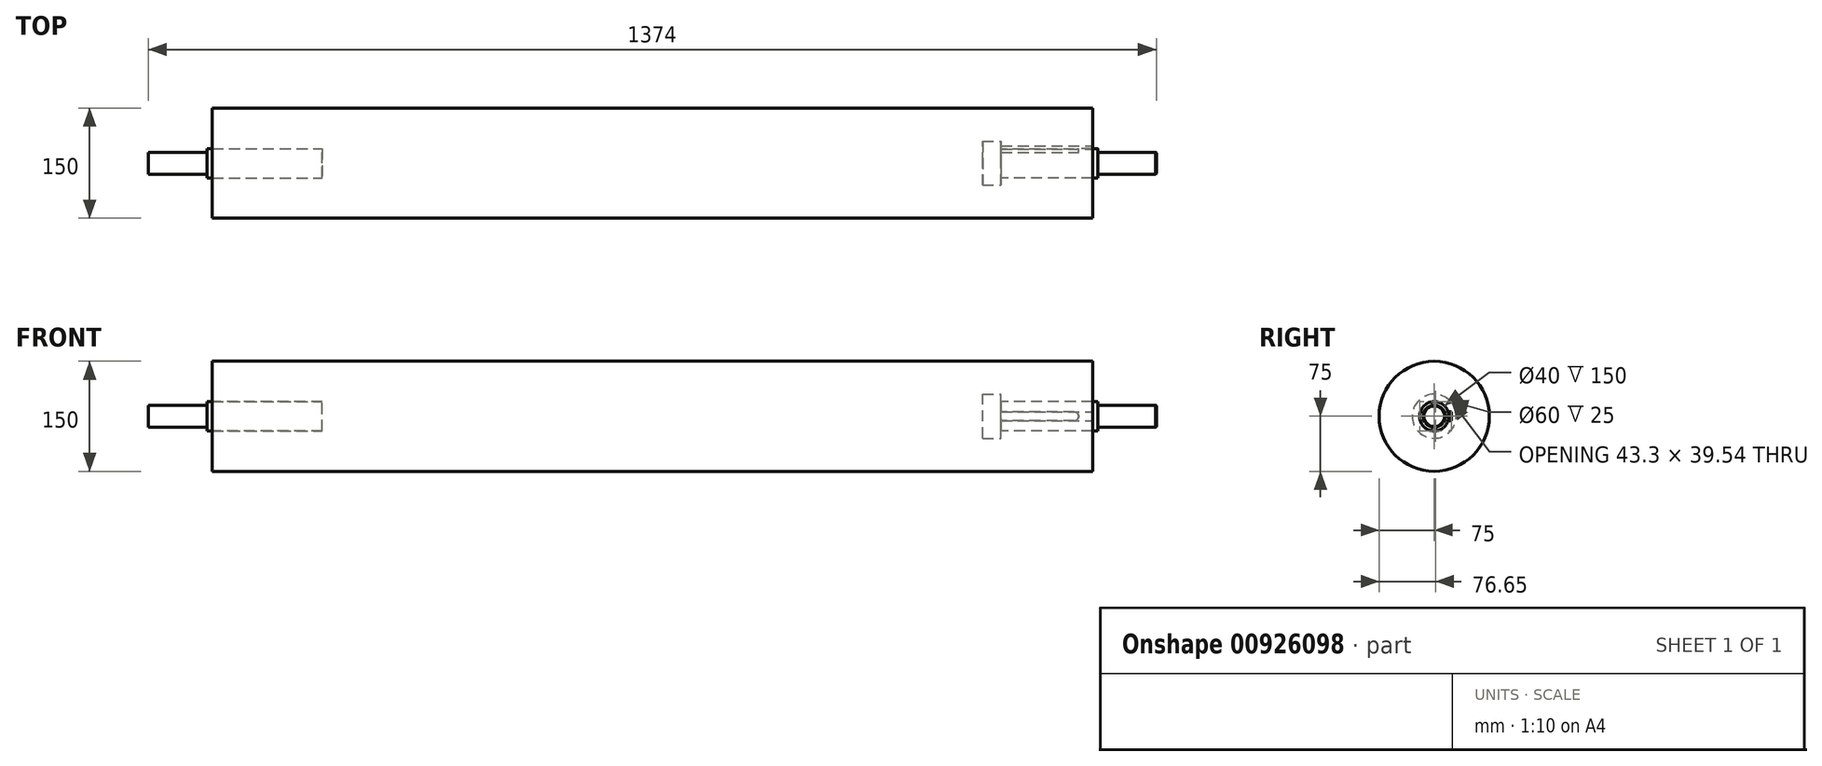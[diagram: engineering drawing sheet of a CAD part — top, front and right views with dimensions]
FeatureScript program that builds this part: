
annotation { "Feature Type Name" : "Feature", "Feature Type Description" : "" }
export const myFeature = defineFeature(function(context is Context, id is Id, definition is map)
    precondition{}
    {
        {
            var Q0;
            Q0=qCreatedBy(makeId("Right.planeOp"),FACE);
            var sketch = newSketch(context, id + "F0", { "sketchPlane" : qUnion([Q0])});
            skCircle(sketch, "E0", {"center": v(0, 0) * mm, "radius": 75 * mm});
            skSolve(sketch);
        }
        {
            var Q0;
            Q0=qSketchRegion(id+"F0",true);
            extrude(context, id + "F1", {"entities" : qUnion([Q0]), "endBound" : BoundingType.SYMMETRIC, "depth" : 1200 * mm, "offsetDistance" : 25 * mm});
        }
        {
            var Q0;
            Q0=makeQuery(id+"F1.opExtrude","CAP_FACE",FACE,{"disambiguationData":[OSD([sQuery(id+"F0.wireOp",EDGE,"E0")])],"isStart":false});
            var sketch = newSketch(context, id + "F2", { "sketchPlane" : qUnion([Q0])});
            skCircle(sketch, "E1", {"center": v(0, 0) * mm, "radius": 20 * mm});
            skSolve(sketch);
        }
        {
            var Q0;
            Q0=qSketchRegion(id+"F2",true);
            extrude(context, id + "F3", {"entities" : qUnion([Q0]), "operationType" : NewBodyOperationType.REMOVE, "oppositeDirection" : true, "depth" : 150 * mm, "offsetDistance" : 25 * mm});
        }
        {
            var Q0;
            Q0=makeQuery(id+"F1.opExtrude","CAP_FACE",FACE,{"disambiguationData":[OSD([sQuery(id+"F0.wireOp",EDGE,"E0")])],"isStart":true});
            var sketch = newSketch(context, id + "F4", { "sketchPlane" : qUnion([Q0])});
            skCircle(sketch, "E2", {"center": v(0, 0) * mm, "radius": 20 * mm});
            skSolve(sketch);
        }
        {
            var Q0;
            Q0=qSketchRegion(id+"F4",true);
            extrude(context, id + "F5", {"entities" : qUnion([Q0]), "operationType" : NewBodyOperationType.REMOVE, "oppositeDirection" : true, "depth" : 150 * mm, "offsetDistance" : 25 * mm});
        }
        {
            var Q0;
            Q0=makeQuery(id+"F1.opExtrude","CAP_FACE",FACE,{"disambiguationData":[OSD([sQuery(id+"F0.wireOp",EDGE,"E0")])],"isStart":false});
            var sketch = newSketch(context, id + "F6", { "sketchPlane" : qUnion([Q0])});
            skLineSegment(sketch, "E3.bottom", {"start": v(19.08, 6) * mm, "end": v(23.3, 6) * mm});
            skLineSegment(sketch, "E3.top", {"start": v(19.08, -6) * mm, "end": v(23.3, -6) * mm});
            skLineSegment(sketch, "E3.left", {"start": v(19.08, 6) * mm, "end": v(19.08, -6) * mm});
            skLineSegment(sketch, "E3.right", {"start": v(23.3, 6) * mm, "end": v(23.3, -6) * mm});
            skPoint(sketch, "E3.middle", {"position": v(21.19, 0) * mm});
            skSolve(sketch);
        }
        {
            var Q0;
            Q0=qSketchRegion(id+"F6",true);
            extrude(context, id + "F7", {"entities" : qUnion([Q0]), "operationType" : NewBodyOperationType.REMOVE, "oppositeDirection" : true, "depth" : 125 * mm, "offsetDistance" : 25 * mm});
        }
        {
            var Q0;
            Q0=makeQuery(id+"F3.boolean.opBoolean","COPY",FACE,{"derivedFrom":makeQuery(id+"F3.opExtrude","CAP_FACE",FACE,{"disambiguationData":[OSD([sQuery(id+"F2.wireOp",EDGE,"E1")])],"isStart":false})});
            var sketch = newSketch(context, id + "F8", { "sketchPlane" : qUnion([Q0])});
            skCircle(sketch, "E4", {"center": v(0, 0) * mm, "radius": 20 * mm});
            skSolve(sketch);
        }
        {
            var Q0;
            Q0=qSketchRegion(id+"F8",true);
            extrude(context, id + "F9", {"entities" : qUnion([Q0]), "depth" : (182 - 25) * mm, "offsetDistance" : 25 * mm});
        }
        {
            var Q0;
            Q0=makeQuery(id+"F9.opExtrude","CAP_FACE",FACE,{"disambiguationData":[OSD([sQuery(id+"F8.wireOp",EDGE,"E4")])],"isStart":false});
            var sketch = newSketch(context, id + "F10", { "sketchPlane" : qUnion([Q0])});
            skCircle(sketch, "E5", {"center": v(0, 0) * mm, "radius": 15 * mm});
            skSolve(sketch);
        }
        {
            var Q0;
            Q0=qSketchRegion(id+"F10",true);
            extrude(context, id + "F11", {"entities" : qUnion([Q0]), "operationType" : NewBodyOperationType.ADD, "depth" : 80 * mm, "offsetDistance" : 25 * mm});
        }
        {
            var Q0;
            Q0=makeQuery(id+"F9.opExtrude","SWEPT_BODY",BODY,{"disambiguationData":[OSD([sQuery(id+"F8.wireOp",EDGE,"E4")])]});
            var Q1;
            Q1=qCreatedBy(makeId("Right.planeOp"),FACE);
            mirror(context, id + "F12", {"entities" : qUnion([Q0]), "mirrorPlane" : qUnion([Q1])});
        }
        {
            var Q0;
            Q0=makeQuery(id+"F7.boolean.opBoolean","COPY",FACE,{"derivedFrom":makeQuery(id+"F7.opExtrude","SWEPT_FACE",FACE,{"disambiguationData":[OSD([sQuery(id+"F6.wireOp",EDGE,"E3.right")])]})});
            var sketch = newSketch(context, id + "F13", { "sketchPlane" : qUnion([Q0])});
            skLineSegment(sketch, "E6", {"start": v(475, 0) * mm, "end": v(575, 0) * mm});
            skArc(sketch, "E7.0.startCap", {"start": v(475, -6) * mm, "mid": v(469, 0) * mm, "end": v(475, 6) * mm});
            skArc(sketch, "E7.0.endCap", {"start": v(575, 6) * mm, "mid": v(581, 0) * mm, "end": v(575, -6) * mm});
            skLineSegment(sketch, "E7.0.left", {"start": v(475, 6) * mm, "end": v(575, 6) * mm});
            skLineSegment(sketch, "E7.0.right", {"start": v(475, -6) * mm, "end": v(575, -6) * mm});
            skSolve(sketch);
        }
        {
            var Q0;
            Q0=qSketchRegion(id+"F13",true);
            extrude(context, id + "F14", {"entities" : qUnion([Q0]), "operationType" : NewBodyOperationType.REMOVE, "depth" : 8.8 * mm, "offsetDistance" : 25 * mm});
        }
        {
            var Q0;
            Q0=makeQuery(id+"F1.opExtrude","CAP_FACE",FACE,{"disambiguationData":[OSD([sQuery(id+"F0.wireOp",EDGE,"E0")])],"isStart":false});
            cPlane(context, id + "F15", {"entities" : qUnion([Q0]), "cplaneType" : CPlaneType.OFFSET, "offset" : 125 * mm, "oppositeDirection" : true, "width" : 150 * mm, "height" : 150 * mm});
        }
        {
            var Q0;
            Q0=qCreatedBy(id+"F15.planeOp",FACE);
            var sketch = newSketch(context, id + "F16", { "sketchPlane" : qUnion([Q0])});
            skCircle(sketch, "E8", {"center": v(0, 0) * mm, "radius": 30 * mm});
            skSolve(sketch);
        }
        {
            var Q0;
            Q0=qSketchRegion(id+"F16",true);
            extrude(context, id + "F17", {"entities" : qUnion([Q0]), "operationType" : NewBodyOperationType.REMOVE, "oppositeDirection" : true, "depth" : 25 * mm, "offsetDistance" : 25 * mm});
        }
        {
            var Q0;
            Q0=makeQuery(id+"F12.opPattern","COPY",FACE,{"derivedFrom":makeQuery(id+"F11.opExtrude","CAP_FACE",FACE,{"disambiguationData":[OSD([sQuery(id+"F10.wireOp",EDGE,"E5")])],"isStart":false}),"instanceName":"1"});
            extrude(context, id + "F18", {"entities" : qUnion([Q0]), "operationType" : NewBodyOperationType.ADD, "oppositeDirection" : true, "depth" : (67 + 25) * mm, "offsetDistance" : 25 * mm});
        }
        {
            var Q0;
            Q0=makeQuery(id+"F18.boolean.opBoolean","COPY",EDGE,{"derivedFrom":makeQuery(id+"F18.opExtrude","CAP_EDGE",EDGE,{"disambiguationData":[OSD([sQuery(id+"F10.wireOp",EDGE,"E5")])],"isStart":false})});
            var Q1;
            Q1=makeQuery(id+"F11.opExtrude","CAP_EDGE",EDGE,{"disambiguationData":[OSD([sQuery(id+"F10.wireOp",EDGE,"E5")])],"isStart":false});
            chamfer(context, id + "F19", {"entities" : qUnion([Q0, Q1]), "width" : 1 * mm, "tangentPropagation" : true});
        }
    });
